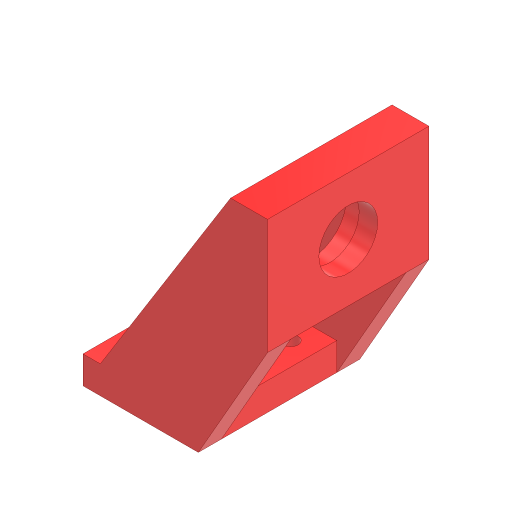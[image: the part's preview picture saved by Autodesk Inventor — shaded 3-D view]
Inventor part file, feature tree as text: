
AUTODESK INVENTOR PART (.ipt)
format: ipt  version: 2024.3 (Build 283343000, 343)  size: 375,808 bytes
history: native  units: mm
features: projected_geometry x7, sketch x6, extrude x5, mirror x1, hole x1
ambient origin geometry x8: Origin, YZ Plane, XZ Plane, XY Plane, X Axis, Y Axis, Z Axis, Center Point
bodies: Solid1 (feature_tree)
feature tree (20):
  extrude  "Extrusion1"  Depth=70.0mm
  extrude  "Extrusion2"  Depth=16.0mm
  extrude  "Extrusion3"  Depth=25.5mm
  extrude  "Extrusion4"  Depth=8.0mm
  mirror  "Mirror1"
  extrude  "Extrusion5"  Depth=50.0mm
  hole  "Hole1"  [1 undecoded]
  sketch  "Sketch1"  dims[d0=50.0mm d1=70.0mm]
  sketch  "Sketch2"  dims[d2=16.0mm d3=0.0mm d4=30.5mm]
  sketch  "Sketch3"  dims[d5=0.0mm d6=0.0mm d7=25.5mm]
  sketch  "Sketch4"  dims[d8=8.0mm d9=0.0mm d10=77.5mm]
  projected_geometry  "Projected Loop1"
  projected_geometry  "Projected Loop2"
  sketch  "Sketch5"  dims[d11=80.0mm d12=50.0mm]
  projected_geometry  "Projected Loop3"
  projected_geometry  "Projected Loop4"
  sketch  "Sketch6"  dims[d13=10.0mm d14=0.0mm d15=12.0mm d16=0.0mm d17=30.0mm d18=30.0mm d19=6.6mm d20=6.0mm d21=12.6mm d22=2.0mm d23=90.0deg d24=8.0mm d25=20.594885mm]
  projected_geometry  "Projected Loop5"
  projected_geometry  "Projected Loop6"
  projected_geometry  "Projected Loop7"
note: 1 required parameter value undecoded (feature->parameter linkage not recoverable at this tier; creation-order binding heuristic only, values carry confidence <= 0.55)
